# Revit family: AccessLadder-Sayfa-LD36-2
name_source: partatom
category: Specialty Equipment
revit_build: Autodesk Revit 2015 (Build: 20150704_0715(x64)
units: mm (PartAtom-declared; Revit-internal decimal feet)

## types (2) — shared parameters
Assembly Code = B1010700
Manufacturer = SAYFA
Material = Metal_Ladders_Aluminium
MaterialPerforated = Metal_Ladders_Aluminium_Perforated
Model = LD36
ModifiedIssue_ANZRS = 20150713.01 $
URL = www.sayfa.com.au
VerticalHeightMaximum = 11600 mm  [stored 38.0577 ft]
VerticalHeightMinimum = 6800 mm  [stored 22.3097 ft]

## per-type parameters (varying)
| type | Description | SupportLanding | SupportLandingOffset |
| Type 1 - Flat Surface to Roof Deck | Angled Cage Ladder with Midway and Top Landing Platform | No | 0 mm  [stored 0 ft] |
| Type 2 - Roof Deck to Roof Deck | Angled Cage Ladder with Midway and Top Landing Platform, and Support Landing | Yes | 77 mm |

note: [stored X ft] marks values corroborated as IEEE doubles in the binary element streams (Revit-internal decimal feet)

## geometry (parser evidence)
native form markers: Sweep x25
no freeform markers — native parametric forms only
